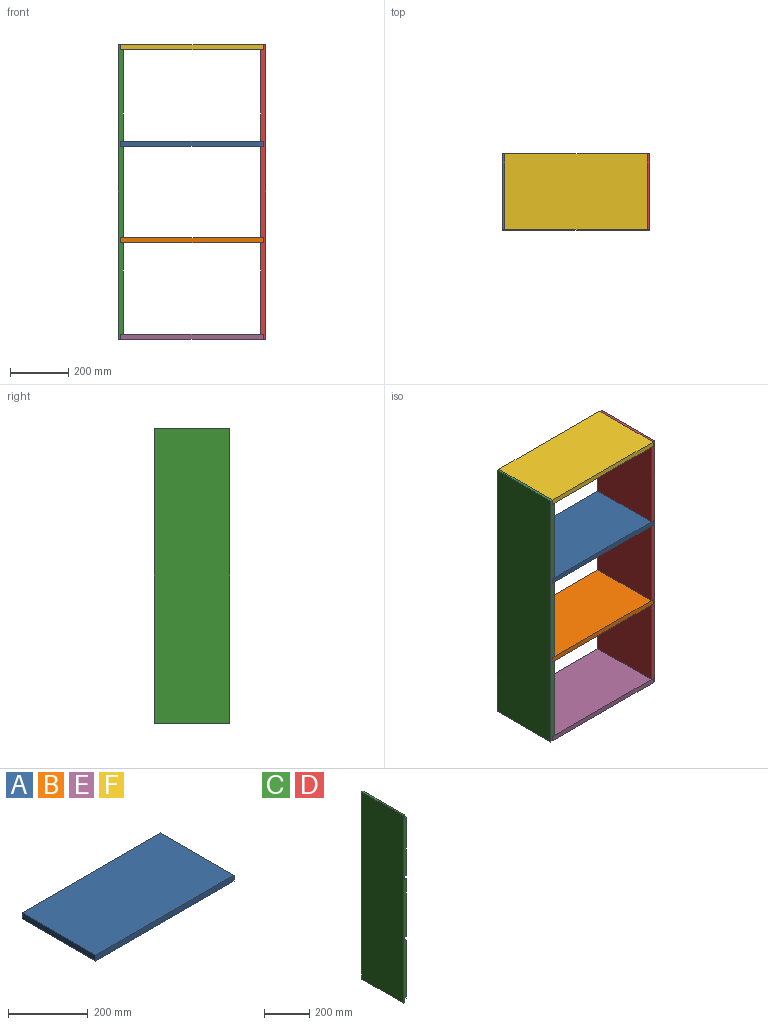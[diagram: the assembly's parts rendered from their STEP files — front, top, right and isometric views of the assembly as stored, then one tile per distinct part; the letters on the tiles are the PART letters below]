
ASSEMBLY  parts=6 mates=5
PART A: 6 faces, bbox 490x260x18 mm
  f0: plane 490x260mm, normal (0,0,1), area 127400mm2, adj f1,f3,f4,f5
  f1: plane 260x18mm, normal (-1,0,0), area 4680mm2, adj f0,f2,f4,f5
  f2: plane 490x260mm, normal (0,0,-1), area 127400mm2, adj f1,f3,f4,f5
  f3: plane 260x18mm, normal (1,0,0), area 4680mm2, adj f0,f2,f4,f5
  f4: plane 490x18mm, normal (0,-1,0), area 8820mm2, adj f0,f1,f2,f3
  f5: plane 490x18mm, normal (0,1,0), area 8820mm2, adj f0,f1,f2,f3
PART B: same geometry as A
PART C: 18 faces, bbox 18x260x1014 mm
  f0: plane 260x18mm, normal (1,0,0), area 4680mm2, adj f1,f15,f16,f17
  f1: plane 260x9mm, normal (0,0,-1), area 2340mm2, adj f0,f2,f16,f17
  f2: plane 314x260mm, normal (1,0,0), area 81640mm2, adj f1,f3,f16,f17
  f3: plane 260x9mm, normal (0,0,1), area 2340mm2, adj f2,f4,f16,f17
  f4: plane 260x18mm, normal (1,0,0), area 4680mm2, adj f3,f5,f16,f17
  f5: plane 260x9mm, normal (0,0,-1), area 2340mm2, adj f4,f6,f16,f17
  f6: plane 314x260mm, normal (1,0,0), area 81640mm2, adj f5,f7,f16,f17
  f7: plane 260x9mm, normal (0,0,1), area 2340mm2, adj f6,f8,f16,f17
  f8: plane 260x18mm, normal (1,0,0), area 4680mm2, adj f7,f9,f16,f17
  f9: plane 260x9mm, normal (0,0,-1), area 2340mm2, adj f8,f10,f16,f17
  f10: plane 314x260mm, normal (1,0,0), area 81640mm2, adj f9,f11,f16,f17
  f11: plane 260x9mm, normal (0,0,1), area 2340mm2, adj f10,f12,f16,f17
  f12: plane 260x18mm, normal (1,0,0), area 4680mm2, adj f11,f13,f16,f17
  f13: plane 260x9mm, normal (0,0,1), area 2340mm2, adj f12,f14,f16,f17
  f14: plane 1014x260mm, normal (-1,0,0), area 263640mm2, adj f13,f15,f16,f17
  f15: plane 260x9mm, normal (0,0,-1), area 2340mm2, adj f0,f14,f16,f17
  f16: plane 1014x18mm, normal (0,-1,0), area 17604mm2, adj f0,f1,f2,f3,f4,f5,f6,f7
  f17: plane 1014x18mm, normal (0,1,0), area 17604mm2, adj f0,f1,f2,f3,f4,f5,f6,f7
PART D: same geometry as C
PART E: same geometry as A
PART F: same geometry as A
PLACE A t=(-275.45,129.34,-167.59)mm
PLACE B t=(-275.45,129.34,-499.59)mm
PLACE C t=(-275.45,129.34,-167.59)mm
PLACE D rot(axis=(0,1,0),180deg) t=(232.55,129.34,846.41)mm
PLACE E t=(-275.45,129.34,-831.59)mm
PLACE F t=(-275.45,129.34,164.41)mm
MATE fastened F.f4 <-> C.f16  axis (0,-1,0) through (-266.45,-130.66,828.41)mm
MATE fastened C.f16 <-> A.f4  axis (0,-1,0) through (-266.45,-130.66,514.41)mm
MATE fastened E.f4 <-> C.f16  axis (0,-1,0) through (-266.45,-130.66,-149.59)mm
MATE fastened C.f16 <-> B.f4  axis (0,-1,0) through (-266.45,-130.66,182.41)mm
MATE fastened F.f4 <-> D.f16  axis (0,-1,0) through (223.55,-130.66,828.41)mm
